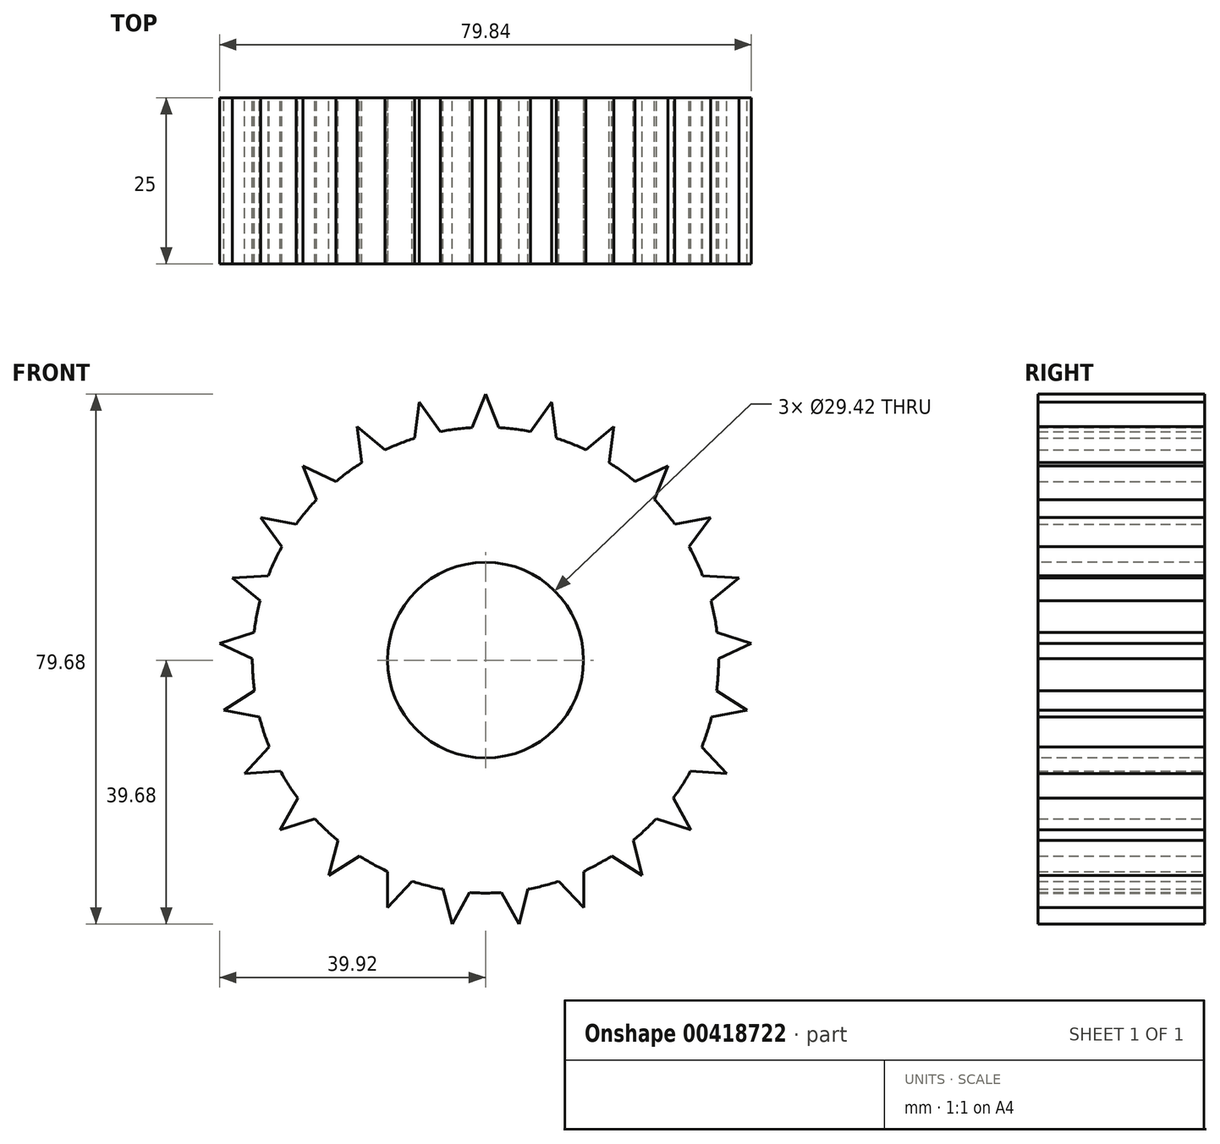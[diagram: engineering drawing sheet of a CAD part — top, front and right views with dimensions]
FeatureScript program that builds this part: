
annotation { "Feature Type Name" : "Feature", "Feature Type Description" : "" }
export const myFeature = defineFeature(function(context is Context, id is Id, definition is map)
    precondition{}
    {
        {
            var Q0;
            Q0=qCreatedBy(makeId("Front.planeOp"),FACE);
            var sketch = newSketch(context, id + "F0", { "sketchPlane" : qUnion([Q0])});
            skCircle(sketch, "E0", {"center": v(0, 0) * mm, "radius": 35 * mm});
            skPoint(sketch, "E1", {"position": v(0, 35) * mm});
            skLineSegment(sketch, "E2", {"start": v(0, 41.27) * mm, "end": v(0, 32.09) * mm, "construction": true});
            skLineSegment(sketch, "E3", {"start": v(0, 40) * mm, "end": v(-2, 34.94) * mm});
            skLineSegment(sketch, "E4.MirrorCS", {"start": v(0, 40) * mm, "end": v(2, 34.94) * mm});
            skLineSegment(sketch, "E5.1.0", {"start": v(-9.95, 38.74) * mm, "end": v(-10.63, 33.35) * mm});
            skLineSegment(sketch, "E5.1.1", {"start": v(-9.95, 38.74) * mm, "end": v(-6.75, 34.34) * mm});
            skLineSegment(sketch, "E5.2.0", {"start": v(-19.27, 35.05) * mm, "end": v(-18.59, 29.66) * mm});
            skLineSegment(sketch, "E5.2.1", {"start": v(-19.27, 35.05) * mm, "end": v(-15.08, 31.58) * mm});
            skLineSegment(sketch, "E5.3.0", {"start": v(-27.38, 29.16) * mm, "end": v(-25.38, 24.1) * mm});
            skLineSegment(sketch, "E5.3.1", {"start": v(-27.38, 29.16) * mm, "end": v(-22.46, 26.84) * mm});
            skLineSegment(sketch, "E5.4.0", {"start": v(-33.77, 21.43) * mm, "end": v(-30.57, 17.03) * mm});
            skLineSegment(sketch, "E5.4.1", {"start": v(-33.77, 21.43) * mm, "end": v(-28.43, 20.41) * mm});
            skLineSegment(sketch, "E5.5.0", {"start": v(-38.04, 12.36) * mm, "end": v(-33.85, 8.9) * mm});
            skLineSegment(sketch, "E5.5.1", {"start": v(-38.04, 12.36) * mm, "end": v(-32.61, 12.7) * mm});
            skLineSegment(sketch, "E5.6.0", {"start": v(-39.92, 2.51) * mm, "end": v(-35, 0.2) * mm});
            skLineSegment(sketch, "E5.6.1", {"start": v(-39.92, 2.51) * mm, "end": v(-34.75, 4.2) * mm});
            skLineSegment(sketch, "E5.7.0", {"start": v(-39.3, -7.5) * mm, "end": v(-33.95, -8.51) * mm});
            skLineSegment(sketch, "E5.7.1", {"start": v(-39.3, -7.5) * mm, "end": v(-34.7, -4.58) * mm});
            skLineSegment(sketch, "E5.8.0", {"start": v(-36.2, -17.03) * mm, "end": v(-30.77, -16.69) * mm});
            skLineSegment(sketch, "E5.8.1", {"start": v(-36.2, -17.03) * mm, "end": v(-32.47, -13.07) * mm});
            skLineSegment(sketch, "E5.9.0", {"start": v(-30.82, -25.5) * mm, "end": v(-25.65, -23.81) * mm});
            skLineSegment(sketch, "E5.9.1", {"start": v(-30.82, -25.5) * mm, "end": v(-28.2, -20.73) * mm});
            skLineSegment(sketch, "E5.10.0", {"start": v(-23.51, -32.36) * mm, "end": v(-18.92, -29.44) * mm});
            skLineSegment(sketch, "E5.10.1", {"start": v(-23.51, -32.36) * mm, "end": v(-22.16, -27.1) * mm});
            skLineSegment(sketch, "E5.11.0", {"start": v(-14.72, -37.2) * mm, "end": v(-11, -33.23) * mm});
            skLineSegment(sketch, "E5.11.1", {"start": v(-14.72, -37.2) * mm, "end": v(-14.72, -31.75) * mm});
            skLineSegment(sketch, "E5.12.0", {"start": v(-5.01, -39.68) * mm, "end": v(-2.4, -34.92) * mm});
            skLineSegment(sketch, "E5.12.1", {"start": v(-5.01, -39.68) * mm, "end": v(-6.36, -34.42) * mm});
            skLineSegment(sketch, "E5.13.0", {"start": v(5.01, -39.68) * mm, "end": v(6.36, -34.42) * mm});
            skLineSegment(sketch, "E5.13.1", {"start": v(5.01, -39.68) * mm, "end": v(2.4, -34.92) * mm});
            skLineSegment(sketch, "E5.14.0", {"start": v(14.72, -37.2) * mm, "end": v(14.72, -31.75) * mm});
            skLineSegment(sketch, "E5.14.1", {"start": v(14.72, -37.2) * mm, "end": v(11, -33.23) * mm});
            skLineSegment(sketch, "E5.15.0", {"start": v(23.51, -32.36) * mm, "end": v(22.16, -27.1) * mm});
            skLineSegment(sketch, "E5.15.1", {"start": v(23.51, -32.36) * mm, "end": v(18.92, -29.44) * mm});
            skLineSegment(sketch, "E5.16.0", {"start": v(30.82, -25.5) * mm, "end": v(28.2, -20.73) * mm});
            skLineSegment(sketch, "E5.16.1", {"start": v(30.82, -25.5) * mm, "end": v(25.65, -23.81) * mm});
            skLineSegment(sketch, "E5.17.0", {"start": v(36.2, -17.03) * mm, "end": v(32.47, -13.07) * mm});
            skLineSegment(sketch, "E5.17.1", {"start": v(36.2, -17.03) * mm, "end": v(30.77, -16.69) * mm});
            skLineSegment(sketch, "E5.18.0", {"start": v(39.3, -7.5) * mm, "end": v(34.7, -4.58) * mm});
            skLineSegment(sketch, "E5.18.1", {"start": v(39.3, -7.5) * mm, "end": v(33.95, -8.51) * mm});
            skLineSegment(sketch, "E5.19.0", {"start": v(39.92, 2.51) * mm, "end": v(34.75, 4.2) * mm});
            skLineSegment(sketch, "E5.19.1", {"start": v(39.92, 2.51) * mm, "end": v(35, 0.2) * mm});
            skLineSegment(sketch, "E6.2.20.0", {"start": v(38.04, 12.36) * mm, "end": v(32.61, 12.7) * mm});
            skLineSegment(sketch, "E6.3.20.0", {"start": v(38.04, 12.36) * mm, "end": v(33.85, 8.9) * mm});
            skLineSegment(sketch, "E6.2.21.0", {"start": v(33.77, 21.43) * mm, "end": v(28.43, 20.41) * mm});
            skLineSegment(sketch, "E6.3.21.0", {"start": v(33.77, 21.43) * mm, "end": v(30.57, 17.03) * mm});
            skLineSegment(sketch, "E6.2.22.0", {"start": v(27.38, 29.16) * mm, "end": v(22.46, 26.84) * mm});
            skLineSegment(sketch, "E6.3.22.0", {"start": v(27.38, 29.16) * mm, "end": v(25.38, 24.1) * mm});
            skLineSegment(sketch, "E6.2.23.0", {"start": v(19.27, 35.05) * mm, "end": v(15.08, 31.58) * mm});
            skLineSegment(sketch, "E6.3.23.0", {"start": v(19.27, 35.05) * mm, "end": v(18.59, 29.66) * mm});
            skLineSegment(sketch, "E6.2.24.0", {"start": v(9.95, 38.74) * mm, "end": v(6.75, 34.34) * mm});
            skLineSegment(sketch, "E6.3.24.0", {"start": v(9.95, 38.74) * mm, "end": v(10.63, 33.35) * mm});
            skSolve(sketch);
        }
        {
            var Q0;
            Q0 = qSketchRegion(id + "F0", true);
            extrude(context, id + "F1", {"entities" : qUnion([Q0]), "depth" : 25 * mm});
        }
        {
            var Q0;
            Q0=makeQuery(id+"F1.opExtrude","CAP_FACE",FACE,{"disambiguationData":[OSD([sQuery(id+"F0.wireOp",EDGE,"E0"),sQuery(id+"F0.wireOp",EDGE,"E3"),sQuery(id+"F0.wireOp",EDGE,"E4.MirrorCS"),sQuery(id+"F0.wireOp",EDGE,"E5.1.0"),sQuery(id+"F0.wireOp",EDGE,"E5.1.1"),sQuery(id+"F0.wireOp",EDGE,"E5.2.0"),sQuery(id+"F0.wireOp",EDGE,"E5.2.1"),sQuery(id+"F0.wireOp",EDGE,"E5.3.0"),sQuery(id+"F0.wireOp",EDGE,"E5.3.1"),sQuery(id+"F0.wireOp",EDGE,"E5.4.0"),sQuery(id+"F0.wireOp",EDGE,"E5.4.1"),sQuery(id+"F0.wireOp",EDGE,"E5.5.0"),sQuery(id+"F0.wireOp",EDGE,"E5.5.1"),sQuery(id+"F0.wireOp",EDGE,"E5.6.0"),sQuery(id+"F0.wireOp",EDGE,"E5.6.1"),sQuery(id+"F0.wireOp",EDGE,"E5.7.0"),sQuery(id+"F0.wireOp",EDGE,"E5.7.1"),sQuery(id+"F0.wireOp",EDGE,"E5.8.0"),sQuery(id+"F0.wireOp",EDGE,"E5.8.1"),sQuery(id+"F0.wireOp",EDGE,"E5.9.0"),sQuery(id+"F0.wireOp",EDGE,"E5.9.1"),sQuery(id+"F0.wireOp",EDGE,"E5.10.0"),sQuery(id+"F0.wireOp",EDGE,"E5.10.1"),sQuery(id+"F0.wireOp",EDGE,"E5.11.0"),sQuery(id+"F0.wireOp",EDGE,"E5.11.1"),sQuery(id+"F0.wireOp",EDGE,"E5.12.0"),sQuery(id+"F0.wireOp",EDGE,"E5.12.1"),sQuery(id+"F0.wireOp",EDGE,"E5.13.0"),sQuery(id+"F0.wireOp",EDGE,"E5.13.1"),sQuery(id+"F0.wireOp",EDGE,"E5.14.0"),sQuery(id+"F0.wireOp",EDGE,"E5.14.1"),sQuery(id+"F0.wireOp",EDGE,"E5.15.0"),sQuery(id+"F0.wireOp",EDGE,"E5.15.1"),sQuery(id+"F0.wireOp",EDGE,"E5.16.0"),sQuery(id+"F0.wireOp",EDGE,"E5.16.1"),sQuery(id+"F0.wireOp",EDGE,"E5.17.0"),sQuery(id+"F0.wireOp",EDGE,"E5.17.1"),sQuery(id+"F0.wireOp",EDGE,"E5.18.0"),sQuery(id+"F0.wireOp",EDGE,"E5.18.1"),sQuery(id+"F0.wireOp",EDGE,"E5.19.0"),sQuery(id+"F0.wireOp",EDGE,"E5.19.1"),sQuery(id+"F0.wireOp",EDGE,"E6.2.20.0"),sQuery(id+"F0.wireOp",EDGE,"E6.3.20.0"),sQuery(id+"F0.wireOp",EDGE,"E6.2.21.0"),sQuery(id+"F0.wireOp",EDGE,"E6.3.21.0"),sQuery(id+"F0.wireOp",EDGE,"E6.2.22.0"),sQuery(id+"F0.wireOp",EDGE,"E6.3.22.0"),sQuery(id+"F0.wireOp",EDGE,"E6.2.23.0"),sQuery(id+"F0.wireOp",EDGE,"E6.3.23.0"),sQuery(id+"F0.wireOp",EDGE,"E6.2.24.0"),sQuery(id+"F0.wireOp",EDGE,"E6.3.24.0")])],"isStart":false});
            var sketch = newSketch(context, id + "F2", { "sketchPlane" : qUnion([Q0])});
            skCircle(sketch, "E7", {"center": v(0, 0) * mm, "radius": 14.71 * mm});
            skSolve(sketch);
        }
        {
            var Q0;
            Q0=makeQuery(id+"F2.imprint","IMPRINT",FACE,{"disambiguationData":[TD([[makeQuery(id+"F2.imprint","IMPRINT",EDGE,{"derivedFrom":sQuery(id+"F2.wireOp",EDGE,"E7")}),1.0]])]});
            var Q1;
            Q1=sQuery(id+"F2.wireOp",EDGE,"E7");
            extrude(context, id + "F3", {"entities" : qUnion([Q0]), "operationType" : NewBodyOperationType.REMOVE, "surfaceEntities" : qUnion([Q1]), "oppositeDirection" : true, "depth" : 123 * mm});
        }
    });
